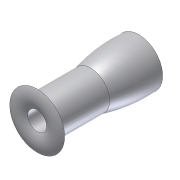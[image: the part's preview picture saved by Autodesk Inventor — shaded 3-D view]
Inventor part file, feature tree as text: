
AUTODESK INVENTOR PART (.ipt)
format: ipt  version: 2012 (Build 160160000, 160)  size: 121,344 bytes
history: native  units: in
note: dims shown in document units (in); Inventor stores cm internally (conversion verified against a paired STEP export)
features: sketch x3, revolve x2, projected_geometry x2, extrude x1, plane x1, other x1
ambient origin geometry x8: Origin, YZ Plane, XZ Plane, XY Plane, X Axis, Y Axis, Z Axis, Center Point
bodies: Solid1 (feature_tree)
feature tree (10):
  extrude  "Extrusion1"  Depth=0.5in TaperAngle=0.0deg
  plane  "Work Plane1"
  revolve  "Revolution1"  Angle=90.0deg
  revolve  "Revolution3"  [1 undecoded]
  sketch  "Sketch1"  dims[d0=0.1875in d1=0.5in d2=0.0in]
  other  "Work Axis1"
  sketch  "Sketch2"  dims[d3=90.0deg d4=90.0deg]
  projected_geometry  "Projected Loop1"
  sketch  "Sketch3"  dims[d6=90.0deg]
  projected_geometry  "Project Cut Edges1"
note: 1 required parameter value undecoded (feature->parameter linkage not recoverable at this tier; creation-order binding heuristic only, values carry confidence <= 0.55)
